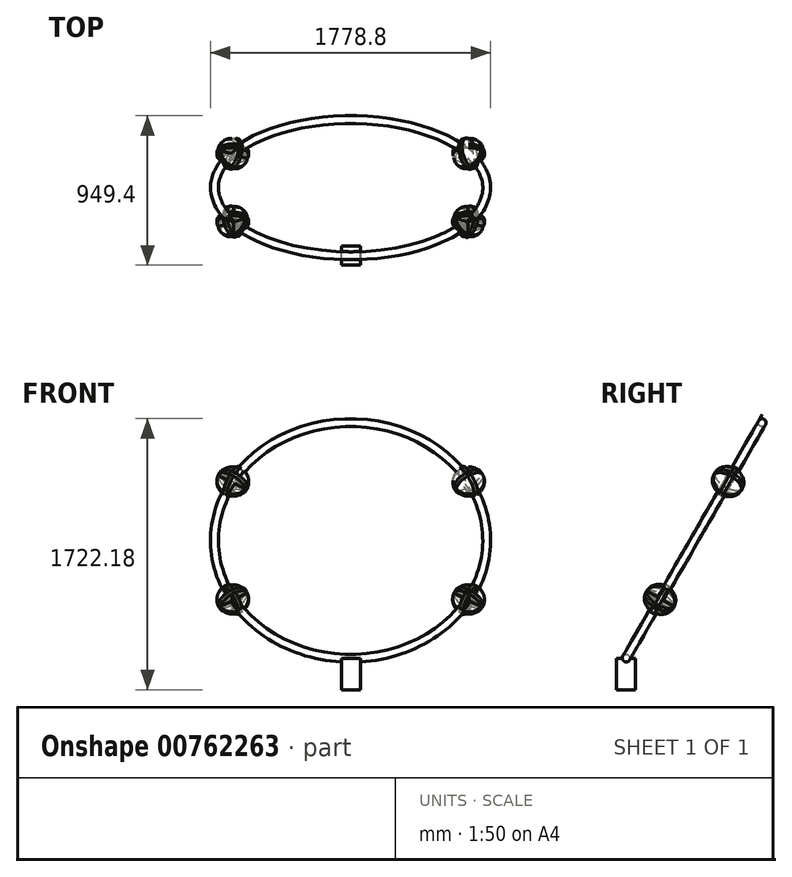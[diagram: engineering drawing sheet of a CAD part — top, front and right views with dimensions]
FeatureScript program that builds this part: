
annotation { "Feature Type Name" : "Feature", "Feature Type Description" : "" }
export const myFeature = defineFeature(function(context is Context, id is Id, definition is map)
    precondition{}
    {
        {
            var Q0;
            Q0=qCreatedBy(makeId("Top.planeOp"),FACE);
            var sketch = newSketch(context, id + "F0", { "sketchPlane" : qUnion([Q0])});
            skLineSegment(sketch, "E0.bottom", {"start": v(60, -60) * mm, "end": v(-60, -60) * mm});
            skLineSegment(sketch, "E0.top", {"start": v(60, 60) * mm, "end": v(-60, 60) * mm});
            skLineSegment(sketch, "E0.left", {"start": v(60, -60) * mm, "end": v(60, 60) * mm});
            skLineSegment(sketch, "E0.right", {"start": v(-60, -60) * mm, "end": v(-60, 60) * mm});
            skPoint(sketch, "E0.middle", {"position": v(0, 0) * mm});
            skSolve(sketch);
        }
        {
            var Q0;
            Q0=makeQuery(id+"F0.imprint","IMPRINT",FACE,{"disambiguationData":[TD([[makeQuery(id+"F0.imprint","IMPRINT",EDGE,{"derivedFrom":sQuery(id+"F0.wireOp",EDGE,"E0.bottom")}),-1.0]])]});
            extrude(context, id + "F1", {"entities" : qUnion([Q0]), "depth" : 0 * mm, "offsetDistance" : 25.4 * mm, "hasSecondDirection" : true, "secondDirectionOppositeDirection" : true, "secondDirectionDepth" : 200 * mm});
        }
        {
            var Q0;
            Q0=qCreatedBy(makeId("Top.planeOp"),FACE);
            var sketch = newSketch(context, id + "F2", { "sketchPlane" : qUnion([Q0])});
            skLineSegment(sketch, "E1", {"start": v(-58.66, 0) * mm, "end": v(56.77, 0) * mm, "construction": true});
            skSolve(sketch);
        }
        {
            var Q0;
            Q0=sQuery(id+"F2.wireOp",EDGE,"E1");
            cPlane(context, id + "F3", {"entities" : qUnion([Q0]), "cplaneType" : CPlaneType.LINE_ANGLE, "offset" : 25.4 * mm, "angle" : 330 * degree, "width" : 152.4 * mm, "height" : 152.4 * mm});
        }
        {
            var Q0;
            Q0=qCreatedBy(id+"F3.planeOp",FACE);
            var sketch = newSketch(context, id + "F4", { "sketchPlane" : qUnion([Q0])});
            skCircle(sketch, "E2", {"center": v(1.67, 864.4) * mm, "radius": 864.4 * mm});
            skPoint(sketch, "E2.first.point", {"position": v(0, 0) * mm});
            skPoint(sketch, "E2.second.point", {"position": v(-773.99, 482.89) * mm});
            skPoint(sketch, "E2.third.point", {"position": v(832.25, 624.98) * mm});
            skLineSegment(sketch, "E3", {"start": v(0, 0) * mm, "end": v(0, 1728.8) * mm});
            skLineSegment(sketch, "E4", {"start": v(0, 0) * mm, "end": v(0, 432.2) * mm});
            skLineSegment(sketch, "E5", {"start": v(0, 0) * mm, "end": v(0, 1296.6) * mm});
            skLineSegment(sketch, "E6", {"start": v(0, 1296.6) * mm, "end": v(-746.92, 1296.6) * mm});
            skLineSegment(sketch, "E7", {"start": v(-746.92, 1296.6) * mm, "end": v(750.26, 1296.6) * mm});
            skLineSegment(sketch, "E8", {"start": v(1.67, 864.4) * mm, "end": v(-862.73, 864.4) * mm});
            skLineSegment(sketch, "E9", {"start": v(-862.73, 864.4) * mm, "end": v(866.07, 864.4) * mm});
            skLineSegment(sketch, "E10", {"start": v(0, 432.2) * mm, "end": v(-746.93, 432.2) * mm});
            skLineSegment(sketch, "E11", {"start": v(-746.93, 432.2) * mm, "end": v(750.26, 432.2) * mm});
            skSolve(sketch);
        }
        {
            var Q0;
            Q0=sQuery(id+"F4.wireOp",VERTEX,"E2.first.point");
            var Q1;
            Q1=sQuery(id+"F2.wireOp",EDGE,"E1");
            cPlane(context, id + "F5", {"entities" : qUnion([Q0, Q1]), "cplaneType" : CPlaneType.LINE_POINT, "offset" : 25.4 * mm, "width" : 152.4 * mm, "height" : 152.4 * mm});
        }
        {
            var Q0;
            Q0=qCreatedBy(id+"F5.planeOp",FACE);
            var sketch = newSketch(context, id + "F6", { "sketchPlane" : qUnion([Q0])});
            skCircle(sketch, "E12", {"center": v(0, 0) * mm, "radius": 25 * mm});
            skSolve(sketch);
        }
        {
            var Q0;
            Q0=makeQuery(id+"F6.imprint","IMPRINT",FACE,{"disambiguationData":[TD([[makeQuery(id+"F6.imprint","IMPRINT",EDGE,{"derivedFrom":sQuery(id+"F6.wireOp",EDGE,"E12")}),1.0]])]});
            var Q1;
            Q1=sQuery(id+"F4.wireOp",EDGE,"E2");
            sweep(context, id + "F7", {"operationType" : NewBodyOperationType.ADD, "profiles" : qUnion([Q0]), "path" : qUnion([Q1])});
        }
        {
            var Q0;
            Q0=sQuery(id+"F4.wireOp",VERTEX,"E7.start");
            var Q1;
            Q1=sQuery(id+"F4.wireOp",EDGE,"E2");
            cPlane(context, id + "F8", {"entities" : qUnion([Q0, Q1]), "cplaneType" : CPlaneType.LINE_ANGLE, "offset" : 25.4 * mm, "angle" : 0 * degree, "width" : 152.4 * mm, "height" : 152.4 * mm});
        }
        {
            var Q0;
            Q0=qCreatedBy(id+"F8.planeOp",FACE);
            var sketch = newSketch(context, id + "F9", { "sketchPlane" : qUnion([Q0])});
            skPoint(sketch, "E13", {"position": v(1295.16, 0) * mm});
            skCircle(sketch, "E14", {"center": v(1295.16, 0) * mm, "radius": 100 * mm});
            skSolve(sketch);
        }
        {
            var Q0;
            Q0=makeQuery(id+"F9.imprint","IMPRINT",FACE,{"disambiguationData":[TD([[makeQuery(id+"F9.imprint","IMPRINT",EDGE,{"derivedFrom":sQuery(id+"F9.wireOp",EDGE,"E14")}),1.0]])]});
            extrude(context, id + "F10", {"entities" : qUnion([Q0]), "depth" : 12.7 * mm, "offsetDistance" : 25.4 * mm, "hasSecondDirection" : true, "secondDirectionOppositeDirection" : true, "secondDirectionDepth" : 12.7 * mm});
        }
        {
            var Q0;
            Q0=sQuery(id+"F9.wireOp",VERTEX,"E13");
            var Q1;
            Q1=sQuery(id+"F4.wireOp",EDGE,"E2");
            cPlane(context, id + "F11", {"entities" : qUnion([Q0, Q1]), "cplaneType" : CPlaneType.LINE_POINT, "offset" : 25.4 * mm, "width" : 152.4 * mm, "height" : 152.4 * mm});
        }
        {
            var Q0;
            Q0=qCreatedBy(id+"F11.planeOp",FACE);
            var sketch = newSketch(context, id + "F12", { "sketchPlane" : qUnion([Q0])});
            skPoint(sketch, "E15", {"position": v(-747.56, 1296.74) * mm});
            skCircle(sketch, "E16", {"center": v(-747.56, 1296.74) * mm, "radius": 100 * mm});
            skSolve(sketch);
        }
        {
            var Q0;
            Q0=makeQuery(id+"F12.imprint","IMPRINT",FACE,{"disambiguationData":[TD([[makeQuery(id+"F12.imprint","IMPRINT",EDGE,{"derivedFrom":sQuery(id+"F12.wireOp",EDGE,"E16")}),1.0]])]});
            extrude(context, id + "F13", {"entities" : qUnion([Q0]), "depth" : 12.7 * mm, "offsetDistance" : 25.4 * mm, "hasSecondDirection" : true, "secondDirectionOppositeDirection" : true, "secondDirectionDepth" : 12.7 * mm});
        }
        {
            var Q0;
            {var subQ0=sQuery(id+"F4.wireOp",EDGE,"E7");var subQ1=sQuery(id+"F4.wireOp",EDGE,"E2");var subQ2=makeQuery(id+"F4.imprint","INTERSECT",VERTEX,{"disambiguationData":[OD(0.0)],"derivedFrom":[subQ1,subQ0]});Q0=makeQuery(id+"F4.imprint","IMPRINT",FACE,{"disambiguationData":[TD([[makeQuery(id+"F4.imprint","IMPRINT",EDGE,{"disambiguationData":[TD([[subQ2,-1.0]])],"derivedFrom":subQ1}),1.0]])]});}
            var sketch = newSketch(context, id + "F14", { "sketchPlane" : qUnion([Q0])});
            skSolve(sketch);
        }
        {
            var Q0;
            {var subQ0=sQuery(id+"F4.wireOp",EDGE,"E7");var subQ1=sQuery(id+"F4.wireOp",EDGE,"E2");var subQ2=makeQuery(id+"F4.imprint","INTERSECT",VERTEX,{"disambiguationData":[OD(0.0)],"derivedFrom":[subQ1,subQ0]});Q0=makeQuery(id+"F14.imprint","IMPRINT",FACE,{"disambiguationData":[TD([[makeQuery(id+"F14.imprint","IMPRINT",EDGE,{"derivedFrom":makeQuery(id+"F4.imprint","IMPRINT",EDGE,{"disambiguationData":[TD([[subQ2,-1.0]])],"derivedFrom":subQ1})}),1.0]])]});}
            var sketch = newSketch(context, id + "F15", { "sketchPlane" : qUnion([Q0])});
            skLineSegment(sketch, "E17", {"start": v(0, 862.4) * mm, "end": v(-745.78, 1296.86) * mm});
            skSolve(sketch);
        }
        {
            var Q0;
            Q0=sQuery(id+"F15.wireOp",VERTEX,"E17.end");
            var Q1;
            Q1=sQuery(id+"F15.wireOp",EDGE,"E17");
            cPlane(context, id + "F16", {"entities" : qUnion([Q0, Q1]), "cplaneType" : CPlaneType.LINE_POINT, "offset" : 25.4 * mm, "width" : 152.4 * mm, "height" : 152.4 * mm});
        }
        {
            var Q0;
            Q0=qCreatedBy(id+"F16.planeOp",FACE);
            var sketch = newSketch(context, id + "F17", { "sketchPlane" : qUnion([Q0])});
            skCircle(sketch, "E18", {"center": v(332.41, 666.3) * mm, "radius": 100 * mm});
            skSolve(sketch);
        }
        {
            var Q0;
            Q0 = qSketchRegion(id + "F17", true);
            extrude(context, id + "F18", {"entities" : qUnion([Q0]), "depth" : 12.7 * mm, "offsetDistance" : 25.4 * mm, "hasSecondDirection" : true, "secondDirectionOppositeDirection" : true, "secondDirectionDepth" : 12.7 * mm});
        }
        {
            var Q0;
            Q0=sQuery(id+"F4.wireOp",VERTEX,"E10.end");
            var Q1;
            Q1=sQuery(id+"F4.wireOp",EDGE,"E2");
            cPlane(context, id + "F19", {"entities" : qUnion([Q0, Q1]), "cplaneType" : CPlaneType.CURVE_POINT, "offset" : 25.4 * mm, "width" : 152.4 * mm, "height" : 152.4 * mm});
        }
        {
            var Q0;
            Q0=qCreatedBy(id+"F19.planeOp",FACE);
            var sketch = newSketch(context, id + "F20", { "sketchPlane" : qUnion([Q0])});
            skCircle(sketch, "E19", {"center": v(431.06, 0) * mm, "radius": 100 * mm});
            skSolve(sketch);
        }
        {
            var Q0;
            Q0=makeQuery(id+"F20.imprint","IMPRINT",FACE,{"disambiguationData":[TD([[makeQuery(id+"F20.imprint","IMPRINT",EDGE,{"derivedFrom":sQuery(id+"F20.wireOp",EDGE,"E19")}),1.0]])]});
            extrude(context, id + "F21", {"entities" : qUnion([Q0]), "operationType" : NewBodyOperationType.ADD, "depth" : 12.7 * mm, "offsetDistance" : 25.4 * mm, "hasSecondDirection" : true, "secondDirectionOppositeDirection" : true, "secondDirectionDepth" : 12.7 * mm});
        }
        {
            var Q0;
            Q0=sQuery(id+"F4.wireOp",VERTEX,"E11.end");
            var Q1;
            Q1=sQuery(id+"F4.wireOp",EDGE,"E2");
            cPlane(context, id + "F22", {"entities" : qUnion([Q0, Q1]), "cplaneType" : CPlaneType.CURVE_POINT, "offset" : 25.4 * mm, "width" : 152.4 * mm, "height" : 152.4 * mm});
        }
        {
            var Q0;
            Q0=qCreatedBy(id+"F22.planeOp",FACE);
            var sketch = newSketch(context, id + "F23", { "sketchPlane" : qUnion([Q0])});
            skCircle(sketch, "E20", {"center": v(-433.72, 0) * mm, "radius": 100 * mm});
            skSolve(sketch);
        }
        {
            var Q0;
            Q0=makeQuery(id+"F23.imprint","IMPRINT",FACE,{"disambiguationData":[TD([[makeQuery(id+"F23.imprint","IMPRINT",EDGE,{"derivedFrom":sQuery(id+"F23.wireOp",EDGE,"E20")}),1.0]])]});
            extrude(context, id + "F24", {"entities" : qUnion([Q0]), "operationType" : NewBodyOperationType.ADD, "depth" : 12.7 * mm, "offsetDistance" : 25.4 * mm, "hasSecondDirection" : true, "secondDirectionOppositeDirection" : true, "secondDirectionDepth" : 12.7 * mm});
        }
        {
            var Q0;
            Q0=sQuery(id+"F4.wireOp",EDGE,"E2");
            var Q1;
            Q1=sQuery(id+"F4.wireOp",VERTEX,"E7.end");
            cPlane(context, id + "F25", {"entities" : qUnion([Q0, Q1]), "cplaneType" : CPlaneType.CURVE_POINT, "offset" : 25.4 * mm, "width" : 152.4 * mm, "height" : 152.4 * mm});
        }
        {
            var Q0;
            Q0=qCreatedBy(id+"F25.planeOp",FACE);
            var sketch = newSketch(context, id + "F26", { "sketchPlane" : qUnion([Q0])});
            skCircle(sketch, "E21", {"center": v(-1297.86, 0) * mm, "radius": 100 * mm});
            skSolve(sketch);
        }
        {
            var Q0;
            Q0=makeQuery(id+"F26.imprint","IMPRINT",FACE,{"disambiguationData":[TD([[makeQuery(id+"F26.imprint","IMPRINT",EDGE,{"derivedFrom":sQuery(id+"F26.wireOp",EDGE,"E21")}),1.0]])]});
            var Q1;
            Q1=sQuery(id+"F26.wireOp",EDGE,"E21");
            extrude(context, id + "F27", {"entities" : qUnion([Q0]), "operationType" : NewBodyOperationType.ADD, "surfaceEntities" : qUnion([Q1]), "depth" : 12.7 * mm, "offsetDistance" : 25.4 * mm, "hasSecondDirection" : true, "secondDirectionOppositeDirection" : true, "secondDirectionDepth" : 12.7 * mm});
        }
        {
            var Q0;
            Q0=sQuery(id+"F4.wireOp",EDGE,"E2");
            var Q1;
            Q1=sQuery(id+"F4.wireOp",VERTEX,"E11.start");
            cPlane(context, id + "F28", {"entities" : qUnion([Q0, Q1]), "cplaneType" : CPlaneType.LINE_POINT, "offset" : 25.4 * mm, "width" : 152.4 * mm, "height" : 152.4 * mm});
        }
        {
            var Q0;
            Q0=qCreatedBy(id+"F28.planeOp",FACE);
            var sketch = newSketch(context, id + "F29", { "sketchPlane" : qUnion([Q0])});
            skCircle(sketch, "E22", {"center": v(-747.2, 432.3) * mm, "radius": 100.33 * mm});
            skSolve(sketch);
        }
        {
            var Q0;
            Q0 = qSketchRegion(id + "F29", true);
            extrude(context, id + "F30", {"entities" : qUnion([Q0]), "operationType" : NewBodyOperationType.ADD, "depth" : 12.7 * mm, "offsetDistance" : 25.4 * mm, "hasSecondDirection" : true, "secondDirectionOppositeDirection" : true, "secondDirectionDepth" : 12.7 * mm});
        }
        {
            var Q0;
            Q0=sQuery(id+"F4.wireOp",VERTEX,"E11.end");
            var Q1;
            Q1=sQuery(id+"F4.wireOp",EDGE,"E2");
            cPlane(context, id + "F31", {"entities" : qUnion([Q0, Q1]), "cplaneType" : CPlaneType.LINE_POINT, "offset" : 25.4 * mm, "width" : 152.4 * mm, "height" : 152.4 * mm});
        }
        {
            var Q0;
            Q0=qCreatedBy(id+"F31.planeOp",FACE);
            var sketch = newSketch(context, id + "F32", { "sketchPlane" : qUnion([Q0])});
            skCircle(sketch, "E23", {"center": v(750.26, 432.26) * mm, "radius": 99.98 * mm});
            skSolve(sketch);
        }
        {
            var Q0;
            Q0=makeQuery(id+"F32.imprint","IMPRINT",FACE,{"disambiguationData":[TD([[makeQuery(id+"F32.imprint","IMPRINT",EDGE,{"derivedFrom":sQuery(id+"F32.wireOp",EDGE,"E23")}),1.0]])]});
            extrude(context, id + "F33", {"entities" : qUnion([Q0]), "operationType" : NewBodyOperationType.ADD, "depth" : 12.7 * mm, "offsetDistance" : 25.4 * mm, "hasSecondDirection" : true, "secondDirectionOppositeDirection" : true, "secondDirectionDepth" : 12.7 * mm});
        }
        {
            var Q0;
            Q0=sQuery(id+"F4.wireOp",VERTEX,"E7.end");
            var Q1;
            Q1=sQuery(id+"F4.wireOp",EDGE,"E2");
            cPlane(context, id + "F34", {"entities" : qUnion([Q0, Q1]), "cplaneType" : CPlaneType.LINE_POINT, "offset" : 25.4 * mm, "width" : 152.4 * mm, "height" : 152.4 * mm});
        }
        {
            var Q0;
            Q0=qCreatedBy(id+"F34.planeOp",FACE);
            var sketch = newSketch(context, id + "F35", { "sketchPlane" : qUnion([Q0])});
            skCircle(sketch, "E24", {"center": v(750.2, 1296.6) * mm, "radius": 100.5 * mm});
            skSolve(sketch);
        }
        {
            var Q0;
            Q0 = qSketchRegion(id + "F35", true);
            extrude(context, id + "F36", {"entities" : qUnion([Q0]), "operationType" : NewBodyOperationType.ADD, "depth" : 12.7 * mm, "offsetDistance" : 25.4 * mm, "hasSecondDirection" : true, "secondDirectionOppositeDirection" : true, "secondDirectionDepth" : 12.7 * mm});
        }
        {
            var Q0;
            {var subQ0=sQuery(id+"F4.wireOp",EDGE,"E9");var subQ1=sQuery(id+"F4.wireOp",EDGE,"E2");var subQ2=makeQuery(id+"F4.imprint","INTERSECT",VERTEX,{"disambiguationData":[OD(0.0)],"derivedFrom":[subQ1,subQ0]});Q0=makeQuery(id+"F4.imprint","IMPRINT",FACE,{"disambiguationData":[TD([[makeQuery(id+"F4.imprint","IMPRINT",EDGE,{"disambiguationData":[TD([[subQ2,-1.0]])],"derivedFrom":subQ1}),1.0]])]});}
            var sketch = newSketch(context, id + "F37", { "sketchPlane" : qUnion([Q0])});
            skLineSegment(sketch, "E25", {"start": v(-746.84, 432.2) * mm, "end": v(0, 864.37) * mm});
            skSolve(sketch);
        }
        {
            var Q0;
            Q0=sQuery(id+"F37.wireOp",EDGE,"E25");
            var Q1;
            Q1=sQuery(id+"F4.wireOp",VERTEX,"E11.start");
            cPlane(context, id + "F38", {"entities" : qUnion([Q0, Q1]), "cplaneType" : CPlaneType.LINE_POINT, "offset" : 25.4 * mm, "width" : 152.4 * mm, "height" : 152.4 * mm});
        }
        {
            var Q0;
            Q0=qCreatedBy(id+"F38.planeOp",FACE);
            var sketch = newSketch(context, id + "F39", { "sketchPlane" : qUnion([Q0])});
            skCircle(sketch, "E26", {"center": v(-334.45, 669.35) * mm, "radius": 99.45 * mm});
            skSolve(sketch);
        }
        {
            var Q0;
            Q0 = qSketchRegion(id + "F39", true);
            extrude(context, id + "F40", {"entities" : qUnion([Q0]), "operationType" : NewBodyOperationType.ADD, "depth" : 12.7 * mm, "offsetDistance" : 25.4 * mm, "hasSecondDirection" : true, "secondDirectionOppositeDirection" : true, "secondDirectionDepth" : 12.7 * mm});
        }
        {
            var Q0;
            {var subQ5=sQuery(id+"F4.wireOp",EDGE,"E9");var subQ8=makeQuery(id+"F4.imprint","IMPRINT",VERTEX,{"derivedFrom":subQ5});Q0=makeQuery(id+"F4.imprint","IMPRINT",FACE,{"disambiguationData":[TD([[makeQuery(id+"F4.imprint","IMPRINT",EDGE,{"disambiguationData":[TD([[subQ8,1.0]])],"derivedFrom":subQ5}),1.0]])]});}
            var sketch = newSketch(context, id + "F41", { "sketchPlane" : qUnion([Q0])});
            skLineSegment(sketch, "E27", {"start": v(750.25, 1296.67) * mm, "end": v(0, 864.2) * mm});
            skSolve(sketch);
        }
        {
            var Q0;
            Q0=sQuery(id+"F4.wireOp",VERTEX,"E7.end");
            var Q1;
            Q1=sQuery(id+"F41.wireOp",EDGE,"E27");
            cPlane(context, id + "F42", {"entities" : qUnion([Q0, Q1]), "cplaneType" : CPlaneType.LINE_POINT, "offset" : 25.4 * mm, "width" : 152.4 * mm, "height" : 152.4 * mm});
        }
        {
            var Q0;
            Q0=qCreatedBy(id+"F42.planeOp",FACE);
            var sketch = newSketch(context, id + "F43", { "sketchPlane" : qUnion([Q0])});
            skCircle(sketch, "E28", {"center": v(334.94, 669.6) * mm, "radius": 98.7 * mm});
            skSolve(sketch);
        }
        {
            var Q0;
            Q0 = qSketchRegion(id + "F43", true);
            extrude(context, id + "F44", {"entities" : qUnion([Q0]), "depth" : 12.7 * mm, "offsetDistance" : 25.4 * mm, "hasSecondDirection" : true, "secondDirectionOppositeDirection" : true, "secondDirectionDepth" : 12.7 * mm});
        }
        {
            var Q0;
            {var subQ0=sQuery(id+"F4.wireOp",EDGE,"E9");var subQ3=makeQuery(id+"F4.imprint","IMPRINT",VERTEX,{"derivedFrom":subQ0});Q0=makeQuery(id+"F4.imprint","IMPRINT",FACE,{"disambiguationData":[TD([[makeQuery(id+"F4.imprint","IMPRINT",EDGE,{"disambiguationData":[TD([[subQ3,1.0]])],"derivedFrom":subQ0}),-1.0]])]});}
            var sketch = newSketch(context, id + "F45", { "sketchPlane" : qUnion([Q0])});
            skLineSegment(sketch, "E29", {"start": v(750.28, 432.21) * mm, "end": v(0, 864.4) * mm});
            skSolve(sketch);
        }
        {
            var Q0;
            Q0=sQuery(id+"F4.wireOp",VERTEX,"E11.end");
            var Q1;
            Q1=sQuery(id+"F45.wireOp",EDGE,"E29");
            cPlane(context, id + "F46", {"entities" : qUnion([Q0, Q1]), "cplaneType" : CPlaneType.LINE_POINT, "offset" : 25.4 * mm, "width" : 152.4 * mm, "height" : 152.4 * mm});
        }
        {
            var Q0;
            Q0=qCreatedBy(id+"F46.planeOp",FACE);
            var sketch = newSketch(context, id + "F47", { "sketchPlane" : qUnion([Q0])});
            skCircle(sketch, "E30", {"center": v(335.48, 670.65) * mm, "radius": 98.91 * mm});
            skSolve(sketch);
        }
        {
            var Q0;
            Q0 = qSketchRegion(id + "F47", true);
            extrude(context, id + "F48", {"entities" : qUnion([Q0]), "operationType" : NewBodyOperationType.ADD, "depth" : 12.7 * mm, "offsetDistance" : 25.4 * mm, "hasSecondDirection" : true, "secondDirectionOppositeDirection" : true, "secondDirectionDepth" : 12.7 * mm});
        }
    });
